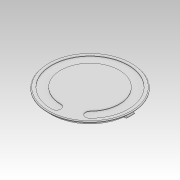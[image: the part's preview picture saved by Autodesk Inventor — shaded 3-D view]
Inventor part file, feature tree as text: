
AUTODESK INVENTOR PART (.ipt)
format: ipt  version: 2020 (Build 240168000, 168)  size: 252,416 bytes
history: native  units: mm
features: other x3, fillet x3, sketch x3, extrude x2, revolve x1, projected_geometry x1
ambient origin geometry x8: Origin, YZ Plane, XZ Plane, XY Plane, X Axis, Y Axis, Z Axis, Center Point
bodies: Solid1 (feature_tree)
feature tree (13):
  other  "Blocks"
  revolve  "Revolution1"  [1 undecoded]
  extrude  "Extrusion1"  Depth=1.4mm
  fillet  "Fillet1"  [1 undecoded]
  extrude  "Extrusion2"  Depth=0.5mm
  fillet  "Fillet2"  Radius=2.0mm
  fillet  "Fillet3"  Radius=0.5mm
  sketch  "Sketch1"  dims[d0=37.35mm d1=3.0mm]
  sketch  "Sketch2"  dims[d2=1.0mm d3=1.4mm d4=120.0deg]
  projected_geometry  "Projected Loop1"
  sketch  "Sketch3"  dims[d5=2.0mm d6=2.0mm d7=2.0mm d8=0.5mm d9=90.0deg d10=8.0mm d11=1.0mm d12=0.0mm d13=1.0mm d14=8.0mm d15=0.4mm d16=0.0mm d17=0.7mm d18=0.5mm]
  other  "Block1"
  other  "Block1:1"
note: 2 required parameter values undecoded (feature->parameter linkage not recoverable at this tier; creation-order binding heuristic only, values carry confidence <= 0.55)